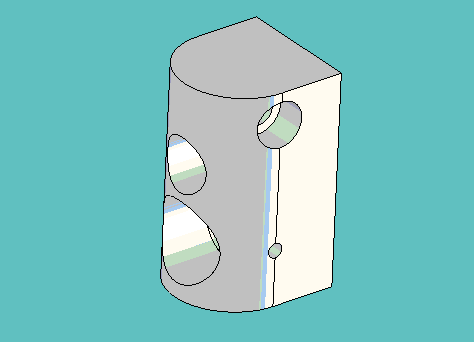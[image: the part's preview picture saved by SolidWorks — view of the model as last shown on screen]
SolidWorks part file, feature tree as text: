
SOLIDWORKS PART (.sldprt)
format: sldprt  version: not decoded by parser v0  size: 314,880 bytes
history: native  units: mm
features: sketch x9, extrude x7, revolve x2, material x1, plane x1, boolean_combine x1 (+11 scaffold rows collapsed)
feature tree (32):
  scaffold x11  (default folders/planes/origin — collapsed)
  material  "Material <not specified>"
  sketch  "Sketch1"  dims[D1=33.3375mm D2=9.525mm D3=153.9875mm]
  revolve  "Revolve1"  Angle=360deg
  sketch  "Sketch14"  dims[D1=10.16mm]
  extrude  "Extrude8"  [1 undecoded]
  sketch  "Sketch2"  dims[c1.D1=3.4544mm c1.D2=2.2606mm c1.D3=8.7376mm c1.D4=28.3464mm c2.D3=8.7376mm c2.D4=28.3464mm]
  extrude  "Extrude1"  [1 undecoded]
  sketch  "Sketch3"  dims[D1=2.2606mm]
  extrude  "Extrude2"  Depth=7.9756mm
  sketch  "Sketch5"  dims[c1.D4=~4.437453mm c1.D5=6.35mm c1.D1=8.7376mm c1.D2=6.35mm c1.D3=6.35mm c2.D4=9.525mm c2.D2=9.525mm c3.D4=9.525mm c3.D6=12.7mm c4.D4=3.175mm]
  revolve  "Revolve2"  Angle=360deg
  sketch  "Sketch11"  dims[D1=~10.31875mm]
  sketch  "Sketch6"  dims[D1=8.5852mm D2=20.6502mm]
  extrude  "Extrude3"  [1 undecoded]
  sketch  "Sketch9"  dims[c1.D1=4.3688mm c1.D2=2.2606mm c1.D3=8.7376mm c1.D4=28.3464mm c2.D3=8.7376mm c2.D4=28.3464mm]
  extrude  "Extrude5"  [1 undecoded]
  plane  "Plane1"  Offset=12.7mm
  sketch  "Sketch10"  dims[D1=~7.14375mm]
  extrude  "Extrude6"  Depth=7.9375mm
  extrude  "Extrude9"  [1 undecoded]
  boolean_combine  "Combine2"
decode coverage: 13 of 19 modeling features carry decoded parameters
note: ~ marks probable driven/reference dimensions
note: 5 parameter values undecoded
summary: no parameter record found for 5 features
note: suppression state not decoded; provenance and decode notes live in map.json
